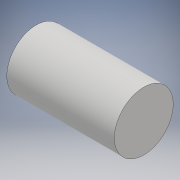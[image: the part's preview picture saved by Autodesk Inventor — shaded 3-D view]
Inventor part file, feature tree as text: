
AUTODESK INVENTOR PART (.ipt)
format: ipt  version: 2018 (Build 220112000, 112)  size: 88,064 bytes
history: native  units: mm
features: extrude x1, sketch x1
ambient origin geometry x8: Origin, YZ Plane, XZ Plane, XY Plane, X Axis, Y Axis, Z Axis, Center Point
bodies: Solid1 (feature_tree)
feature tree (2):
  extrude  "Extrusion1"  [1 undecoded]
  sketch  "Sketch1"  dims[d0=20.0mm d1=0.0mm]
note: 1 required parameter value undecoded (feature->parameter linkage not recoverable at this tier; creation-order binding heuristic only, values carry confidence <= 0.55)
